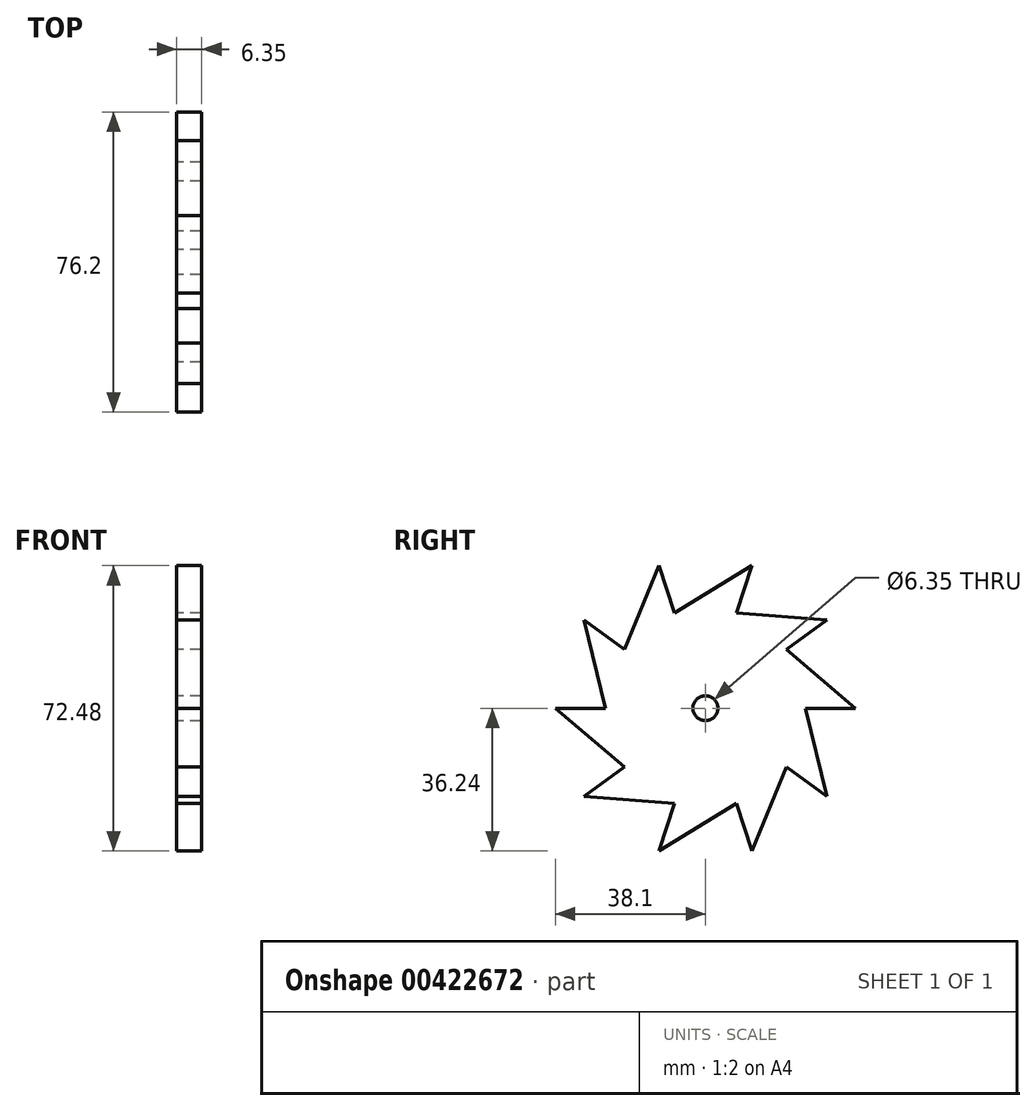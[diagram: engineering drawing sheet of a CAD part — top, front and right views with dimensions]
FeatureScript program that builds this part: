
annotation { "Feature Type Name" : "Feature", "Feature Type Description" : "" }
export const myFeature = defineFeature(function(context is Context, id is Id, definition is map)
    precondition{}
    {
        {
            var Q0;
            Q0=qCreatedBy(makeId("Right.planeOp"),FACE);
            var sketch = newSketch(context, id + "F0", { "sketchPlane" : qUnion([Q0])});
            skCircle(sketch, "E0", {"center": v(0, 0) * mm, "radius": 50.8 * mm});
            skCircle(sketch, "E1", {"center": v(0, 0) * mm, "radius": 38.1 * mm});
            skLineSegment(sketch, "E2", {"start": v(25.4, 0) * mm, "end": v(38.1, 0) * mm});
            skLineSegment(sketch, "E3.1.0", {"start": v(20.55, 14.93) * mm, "end": v(30.82, 22.4) * mm});
            skLineSegment(sketch, "E3.2.0", {"start": v(7.85, 24.16) * mm, "end": v(11.77, 36.24) * mm});
            skLineSegment(sketch, "E3.3.0", {"start": v(-7.85, 24.16) * mm, "end": v(-11.77, 36.24) * mm});
            skLineSegment(sketch, "E3.4.0", {"start": v(-20.55, 14.93) * mm, "end": v(-30.82, 22.4) * mm});
            skLineSegment(sketch, "E3.5.0", {"start": v(-25.4, 0) * mm, "end": v(-38.1, 0) * mm});
            skLineSegment(sketch, "E3.6.0", {"start": v(-20.55, -14.93) * mm, "end": v(-30.82, -22.4) * mm});
            skLineSegment(sketch, "E3.7.0", {"start": v(-7.85, -24.16) * mm, "end": v(-11.77, -36.24) * mm});
            skLineSegment(sketch, "E3.8.0", {"start": v(7.85, -24.16) * mm, "end": v(11.77, -36.24) * mm});
            skLineSegment(sketch, "E3.9.0", {"start": v(20.55, -14.93) * mm, "end": v(30.82, -22.4) * mm});
            skLineSegment(sketch, "E4", {"start": v(38.1, 0) * mm, "end": v(20.55, 14.93) * mm});
            skLineSegment(sketch, "E5.1.0", {"start": v(30.82, 22.4) * mm, "end": v(7.85, 24.16) * mm});
            skLineSegment(sketch, "E5.2.0", {"start": v(11.77, 36.24) * mm, "end": v(-7.85, 24.16) * mm});
            skLineSegment(sketch, "E5.3.0", {"start": v(-11.77, 36.24) * mm, "end": v(-20.55, 14.93) * mm});
            skLineSegment(sketch, "E5.4.0", {"start": v(-30.82, 22.4) * mm, "end": v(-25.4, 0) * mm});
            skLineSegment(sketch, "E5.5.0", {"start": v(-38.1, 0) * mm, "end": v(-20.55, -14.93) * mm});
            skLineSegment(sketch, "E5.6.0", {"start": v(-30.82, -22.4) * mm, "end": v(-7.85, -24.16) * mm});
            skLineSegment(sketch, "E5.7.0", {"start": v(-11.77, -36.24) * mm, "end": v(7.85, -24.16) * mm});
            skLineSegment(sketch, "E5.8.0", {"start": v(11.77, -36.24) * mm, "end": v(20.55, -14.93) * mm});
            skLineSegment(sketch, "E5.9.0", {"start": v(30.82, -22.4) * mm, "end": v(25.4, 0) * mm});
            skLineSegment(sketch, "E6", {"start": v(0, 38.1) * mm, "end": v(0, 50.8) * mm});
            skLineSegment(sketch, "E7.1.0", {"start": v(-22.4, 30.82) * mm, "end": v(-29.86, 41.1) * mm});
            skLineSegment(sketch, "E7.2.0", {"start": v(-36.24, 11.77) * mm, "end": v(-48.31, 15.7) * mm});
            skLineSegment(sketch, "E7.3.0", {"start": v(-36.24, -11.77) * mm, "end": v(-48.31, -15.7) * mm});
            skLineSegment(sketch, "E7.4.0", {"start": v(-22.4, -30.82) * mm, "end": v(-29.86, -41.1) * mm});
            skLineSegment(sketch, "E7.5.0", {"start": v(0, -38.1) * mm, "end": v(0, -50.8) * mm});
            skLineSegment(sketch, "E7.6.0", {"start": v(22.4, -30.82) * mm, "end": v(29.86, -41.1) * mm});
            skLineSegment(sketch, "E7.7.0", {"start": v(36.24, -11.77) * mm, "end": v(48.31, -15.7) * mm});
            skLineSegment(sketch, "E7.8.0", {"start": v(36.24, 11.77) * mm, "end": v(48.31, 15.7) * mm});
            skLineSegment(sketch, "E7.9.0", {"start": v(22.4, 30.82) * mm, "end": v(29.86, 41.1) * mm});
            skLineSegment(sketch, "E8", {"start": v(-48.31, 15.7) * mm, "end": v(-48.31, -15.7) * mm});
            skLineSegment(sketch, "E9.1.0", {"start": v(-48.31, -15.7) * mm, "end": v(-29.86, -41.1) * mm});
            skLineSegment(sketch, "E9.2.0", {"start": v(-29.86, -41.1) * mm, "end": v(0, -50.8) * mm});
            skLineSegment(sketch, "E9.3.0", {"start": v(0, -50.8) * mm, "end": v(29.86, -41.1) * mm});
            skLineSegment(sketch, "E9.4.0", {"start": v(29.86, -41.1) * mm, "end": v(48.31, -15.7) * mm});
            skLineSegment(sketch, "E9.5.0", {"start": v(48.31, -15.7) * mm, "end": v(48.31, 15.7) * mm});
            skLineSegment(sketch, "E9.6.0", {"start": v(48.31, 15.7) * mm, "end": v(29.86, 41.1) * mm});
            skLineSegment(sketch, "E9.7.0", {"start": v(29.86, 41.1) * mm, "end": v(0, 50.8) * mm});
            skLineSegment(sketch, "E9.8.0", {"start": v(0, 50.8) * mm, "end": v(-29.86, 41.1) * mm});
            skLineSegment(sketch, "E9.9.0", {"start": v(-29.86, 41.1) * mm, "end": v(-48.31, 15.7) * mm});
            skCircle(sketch, "E10", {"center": v(0, 0) * mm, "radius": 3.18 * mm});
            skSolve(sketch);
        }
        {
            var Q0;
            Q0=makeQuery(id+"F0.imprint","IMPRINT",FACE,{"disambiguationData":[TD([[makeQuery(id+"F0.imprint","IMPRINT",EDGE,{"derivedFrom":sQuery(id+"F0.wireOp",EDGE,"E2")}),1.0]])]});
            extrude(context, id + "F1", {"entities" : qUnion([Q0]), "depth" : 6.35 * mm});
        }
    });
